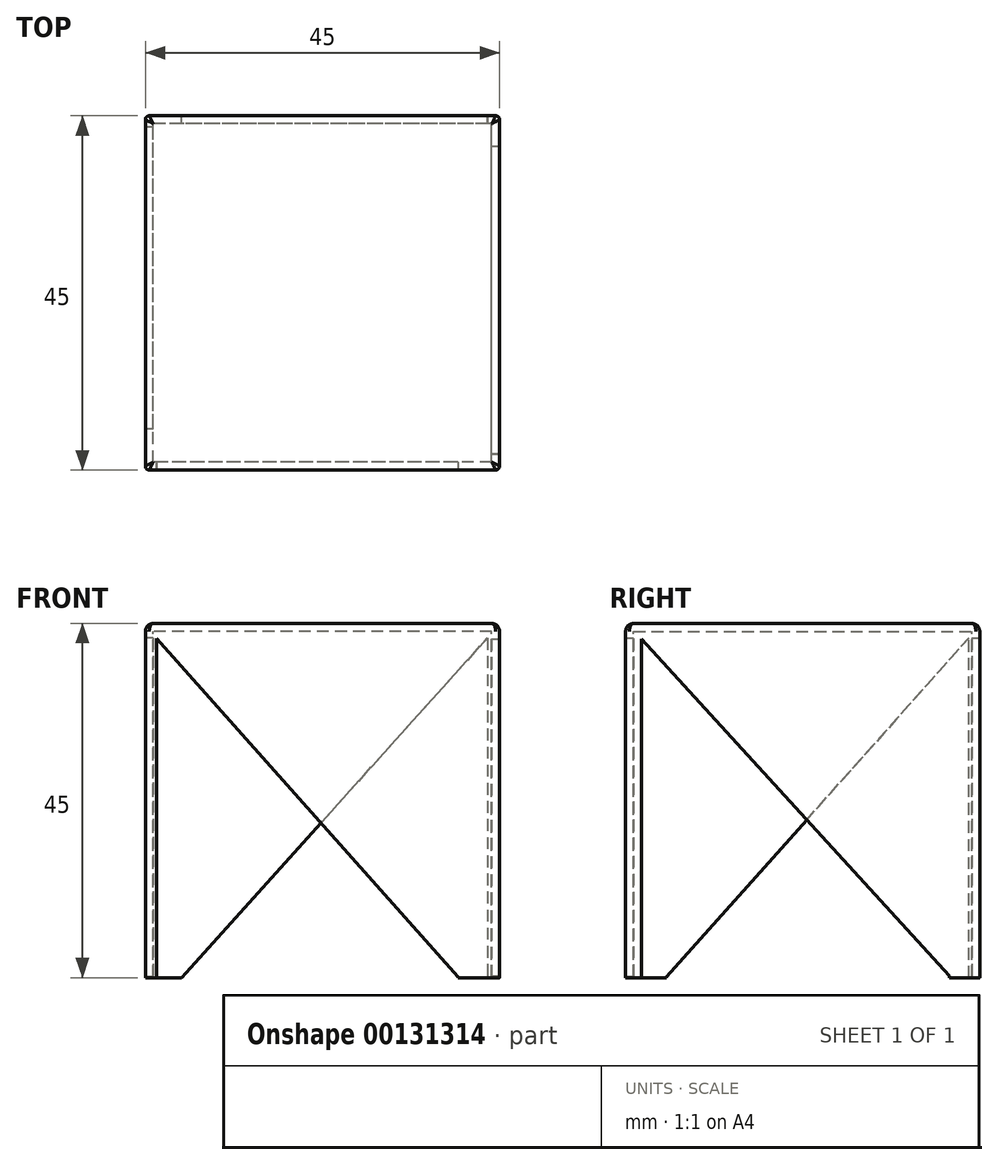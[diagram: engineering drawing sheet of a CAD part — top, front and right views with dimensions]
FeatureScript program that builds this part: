
annotation { "Feature Type Name" : "Feature", "Feature Type Description" : "" }
export const myFeature = defineFeature(function(context is Context, id is Id, definition is map)
    precondition{}
    {
        {
            var Q0;
            Q0=qCreatedBy(makeId("Top.planeOp"),FACE);
            var sketch = newSketch(context, id + "F0", { "sketchPlane" : qUnion([Q0])});
            skLineSegment(sketch, "E0.bottom", {"start": v(22.5, -22.5) * mm, "end": v(-22.5, -22.5) * mm});
            skLineSegment(sketch, "E0.top", {"start": v(22.5, 22.5) * mm, "end": v(-22.5, 22.5) * mm});
            skLineSegment(sketch, "E0.left", {"start": v(22.5, -22.5) * mm, "end": v(22.5, 22.5) * mm});
            skLineSegment(sketch, "E0.right", {"start": v(-22.5, -22.5) * mm, "end": v(-22.5, 22.5) * mm});
            skPoint(sketch, "E0.middle", {"position": v(0, 0) * mm});
            skSolve(sketch);
        }
        {
            var Q0;
            Q0=makeQuery(id+"F0.imprint","IMPRINT",FACE,{"disambiguationData":[TD([[makeQuery(id+"F0.imprint","IMPRINT",EDGE,{"derivedFrom":sQuery(id+"F0.wireOp",EDGE,"E0.bottom")}),-1.0]])]});
            extrude(context, id + "F1", {"entities" : qUnion([Q0]), "endBound" : BoundingType.SYMMETRIC, "depth" : 45 * mm});
        }
        {
            var Q0;
            Q0=qCreatedBy(makeId("Top.planeOp"),FACE);
            cPlane(context, id + "F2", {"entities" : qUnion([Q0]), "cplaneType" : CPlaneType.OFFSET, "offset" : 22 * mm, "oppositeDirection" : true, "width" : 150 * mm, "height" : 150 * mm});
        }
        {
            var Q0;
            Q0=qCreatedBy(id+"F2.planeOp",FACE);
            var sketch = newSketch(context, id + "F3", { "sketchPlane" : qUnion([Q0])});
            skLineSegment(sketch, "E1.bottom", {"start": v(21.5, -21.5) * mm, "end": v(-21.5, -21.5) * mm});
            skLineSegment(sketch, "E1.top", {"start": v(21.5, 21.5) * mm, "end": v(-21.5, 21.5) * mm});
            skLineSegment(sketch, "E1.left", {"start": v(21.5, -21.5) * mm, "end": v(21.5, 21.5) * mm});
            skLineSegment(sketch, "E1.right", {"start": v(-21.5, -21.5) * mm, "end": v(-21.5, 21.5) * mm});
            skPoint(sketch, "E1.middle", {"position": v(0, 0) * mm});
            skSolve(sketch);
        }
        {
            var Q0;
            Q0 = qSketchRegion(id + "F3", true);
            extrude(context, id + "F4", {"entities" : qUnion([Q0]), "operationType" : NewBodyOperationType.REMOVE, "endBound" : BoundingType.SYMMETRIC, "oppositeDirection" : true, "depth" : 86.97 * mm});
        }
        {
            var Q0;
            Q0=makeQuery(id+"F1.opExtrude","SWEPT_FACE",FACE,{"disambiguationData":[OSD([sQuery(id+"F0.wireOp",EDGE,"E0.left")])]});
            cPlane(context, id + "F5", {"entities" : qUnion([Q0]), "cplaneType" : CPlaneType.OFFSET, "offset" : 1 * mm, "width" : 150 * mm, "height" : 150 * mm});
        }
        {
            var Q0;
            Q0=qCreatedBy(id+"F5.planeOp",FACE);
            var sketch = newSketch(context, id + "F6", { "sketchPlane" : qUnion([Q0])});
            skLineSegment(sketch, "E2", {"start": v(-20.48, -22.35) * mm, "end": v(-20.48, 20.55) * mm});
            skLineSegment(sketch, "E3", {"start": v(-20.48, 20.55) * mm, "end": v(18.64, -22.29) * mm});
            skLineSegment(sketch, "E4", {"start": v(18.64, -22.29) * mm, "end": v(18.64, -25.06) * mm});
            skLineSegment(sketch, "E5", {"start": v(18.64, -25.06) * mm, "end": v(-20.78, -25.06) * mm});
            skLineSegment(sketch, "E6", {"start": v(-20.78, -25.06) * mm, "end": v(-20.48, -22.35) * mm});
            skSolve(sketch);
        }
        {
            var Q0;
            Q0=makeQuery(id+"F6.imprint","IMPRINT",FACE,{"disambiguationData":[TD([[makeQuery(id+"F6.imprint","IMPRINT",EDGE,{"derivedFrom":sQuery(id+"F6.wireOp",EDGE,"E2")}),-1.0]])]});
            extrude(context, id + "F7", {"entities" : qUnion([Q0]), "operationType" : NewBodyOperationType.REMOVE, "oppositeDirection" : true, "depth" : 25 * mm});
        }
        {
            var Q0;
            Q0=makeQuery(id+"F1.opExtrude","SWEPT_FACE",FACE,{"disambiguationData":[OSD([sQuery(id+"F0.wireOp",EDGE,"E0.bottom")])]});
            cPlane(context, id + "F8", {"entities" : qUnion([Q0]), "cplaneType" : CPlaneType.OFFSET, "offset" : 1 * mm, "width" : 150 * mm, "height" : 150 * mm});
        }
        {
            var Q0;
            Q0=qCreatedBy(id+"F8.planeOp",FACE);
            var sketch = newSketch(context, id + "F9", { "sketchPlane" : qUnion([Q0])});
            skLineSegment(sketch, "E7", {"start": v(-21.06, -22.47) * mm, "end": v(-21.06, 20.6) * mm});
            skLineSegment(sketch, "E8", {"start": v(-21.06, 20.6) * mm, "end": v(17.2, -22.36) * mm});
            skLineSegment(sketch, "E9", {"start": v(17.2, -22.36) * mm, "end": v(17.3, -25.3) * mm});
            skLineSegment(sketch, "E10", {"start": v(17.3, -25.3) * mm, "end": v(-21.35, -25.3) * mm});
            skLineSegment(sketch, "E11", {"start": v(-21.35, -25.3) * mm, "end": v(-21.06, -22.47) * mm});
            skSolve(sketch);
        }
        {
            var Q0;
            Q0=makeQuery(id+"F9.imprint","IMPRINT",FACE,{"disambiguationData":[TD([[makeQuery(id+"F9.imprint","IMPRINT",EDGE,{"derivedFrom":sQuery(id+"F9.wireOp",EDGE,"E7")}),-1.0]])]});
            extrude(context, id + "F10", {"entities" : qUnion([Q0]), "operationType" : NewBodyOperationType.REMOVE, "oppositeDirection" : true, "depth" : 25 * mm});
        }
        {
            var Q0;
            Q0=makeQuery(id+"F1.opExtrude","SWEPT_FACE",FACE,{"disambiguationData":[OSD([sQuery(id+"F0.wireOp",EDGE,"E0.right")])]});
            cPlane(context, id + "F11", {"entities" : qUnion([Q0]), "cplaneType" : CPlaneType.OFFSET, "offset" : 1 * mm, "width" : 150 * mm, "height" : 150 * mm});
        }
        {
            var Q0;
            Q0=qCreatedBy(id+"F11.planeOp",FACE);
            var sketch = newSketch(context, id + "F12", { "sketchPlane" : qUnion([Q0])});
            skLineSegment(sketch, "E12", {"start": v(-21.12, -23.13) * mm, "end": v(-21.12, 20.68) * mm});
            skLineSegment(sketch, "E13", {"start": v(-21.12, 20.68) * mm, "end": v(17.3, -22.4) * mm});
            skLineSegment(sketch, "E14", {"start": v(17.3, -22.4) * mm, "end": v(17.3, -27.9) * mm});
            skLineSegment(sketch, "E15", {"start": v(17.3, -27.9) * mm, "end": v(-21.12, -23.13) * mm});
            skSolve(sketch);
        }
        {
            var Q0;
            Q0=makeQuery(id+"F12.imprint","IMPRINT",FACE,{"disambiguationData":[TD([[makeQuery(id+"F12.imprint","IMPRINT",EDGE,{"derivedFrom":sQuery(id+"F12.wireOp",EDGE,"E12")}),-1.0]])]});
            extrude(context, id + "F13", {"entities" : qUnion([Q0]), "operationType" : NewBodyOperationType.REMOVE, "oppositeDirection" : true, "depth" : 25 * mm});
        }
        {
            var Q0;
            Q0=makeQuery(id+"F1.opExtrude","SWEPT_FACE",FACE,{"disambiguationData":[OSD([sQuery(id+"F0.wireOp",EDGE,"E0.top")])]});
            cPlane(context, id + "F14", {"entities" : qUnion([Q0]), "cplaneType" : CPlaneType.OFFSET, "offset" : 1 * mm, "width" : 150 * mm, "height" : 150 * mm});
        }
        {
            var Q0;
            Q0=qCreatedBy(id+"F14.planeOp",FACE);
            var sketch = newSketch(context, id + "F15", { "sketchPlane" : qUnion([Q0])});
            skLineSegment(sketch, "E16", {"start": v(-20.94, -22.46) * mm, "end": v(-20.94, 20.65) * mm});
            skLineSegment(sketch, "E17", {"start": v(-20.94, 20.65) * mm, "end": v(17.95, -22.56) * mm});
            skLineSegment(sketch, "E18", {"start": v(17.95, -22.56) * mm, "end": v(18.05, -26.06) * mm});
            skLineSegment(sketch, "E19", {"start": v(18.05, -26.06) * mm, "end": v(-20.73, -26.06) * mm});
            skLineSegment(sketch, "E20", {"start": v(-20.73, -26.06) * mm, "end": v(-20.94, -22.46) * mm});
            skSolve(sketch);
        }
        {
            var Q0;
            Q0=makeQuery(id+"F15.imprint","IMPRINT",FACE,{"disambiguationData":[TD([[makeQuery(id+"F15.imprint","IMPRINT",EDGE,{"derivedFrom":sQuery(id+"F15.wireOp",EDGE,"E16")}),-1.0]])]});
            extrude(context, id + "F16", {"entities" : qUnion([Q0]), "operationType" : NewBodyOperationType.REMOVE, "oppositeDirection" : true, "depth" : 25 * mm});
        }
        {
            var Q0;
            Q0=makeQuery(id+"F1.opExtrude","CAP_EDGE",EDGE,{"disambiguationData":[OSD([sQuery(id+"F0.wireOp",EDGE,"E0.top")])],"isStart":false});
            var Q1;
            Q1=makeQuery(id+"F1.opExtrude","CAP_EDGE",EDGE,{"disambiguationData":[OSD([sQuery(id+"F0.wireOp",EDGE,"E0.left")])],"isStart":false});
            var Q2;
            Q2=makeQuery(id+"F1.opExtrude","CAP_EDGE",EDGE,{"disambiguationData":[OSD([sQuery(id+"F0.wireOp",EDGE,"E0.right")])],"isStart":false});
            var Q3;
            Q3=makeQuery(id+"F1.opExtrude","CAP_EDGE",EDGE,{"disambiguationData":[OSD([sQuery(id+"F0.wireOp",EDGE,"E0.bottom")])],"isStart":false});
            fillet(context, id + "F17", {"entities" : qUnion([Q0, Q1, Q2, Q3]), "radius" : 1 * mm, "tangentPropagation" : true, "allowEdgeOverflow" : false});
        }
        {
            var Q0;
            Q0=makeQuery(id+"F1.opExtrude","SWEPT_EDGE",EDGE,{"disambiguationData":[OSD([sQuery(id+"F0.wireOp",EDGE,"E0.bottom"),sQuery(id+"F0.wireOp",EDGE,"E0.right")])]});
            var Q1;
            Q1=makeQuery(id+"F1.opExtrude","SWEPT_EDGE",EDGE,{"disambiguationData":[OSD([sQuery(id+"F0.wireOp",EDGE,"E0.top"),sQuery(id+"F0.wireOp",EDGE,"E0.right")])]});
            var Q2;
            Q2=makeQuery(id+"F1.opExtrude","SWEPT_EDGE",EDGE,{"disambiguationData":[OSD([sQuery(id+"F0.wireOp",EDGE,"E0.bottom"),sQuery(id+"F0.wireOp",EDGE,"E0.left")])]});
            var Q3;
            Q3=makeQuery(id+"F1.opExtrude","SWEPT_EDGE",EDGE,{"disambiguationData":[OSD([sQuery(id+"F0.wireOp",EDGE,"E0.top"),sQuery(id+"F0.wireOp",EDGE,"E0.left")])]});
            fillet(context, id + "F18", {"entities" : qUnion([Q0, Q1, Q2, Q3]), "radius" : 0.5 * mm, "tangentPropagation" : true, "allowEdgeOverflow" : false});
        }
    });
